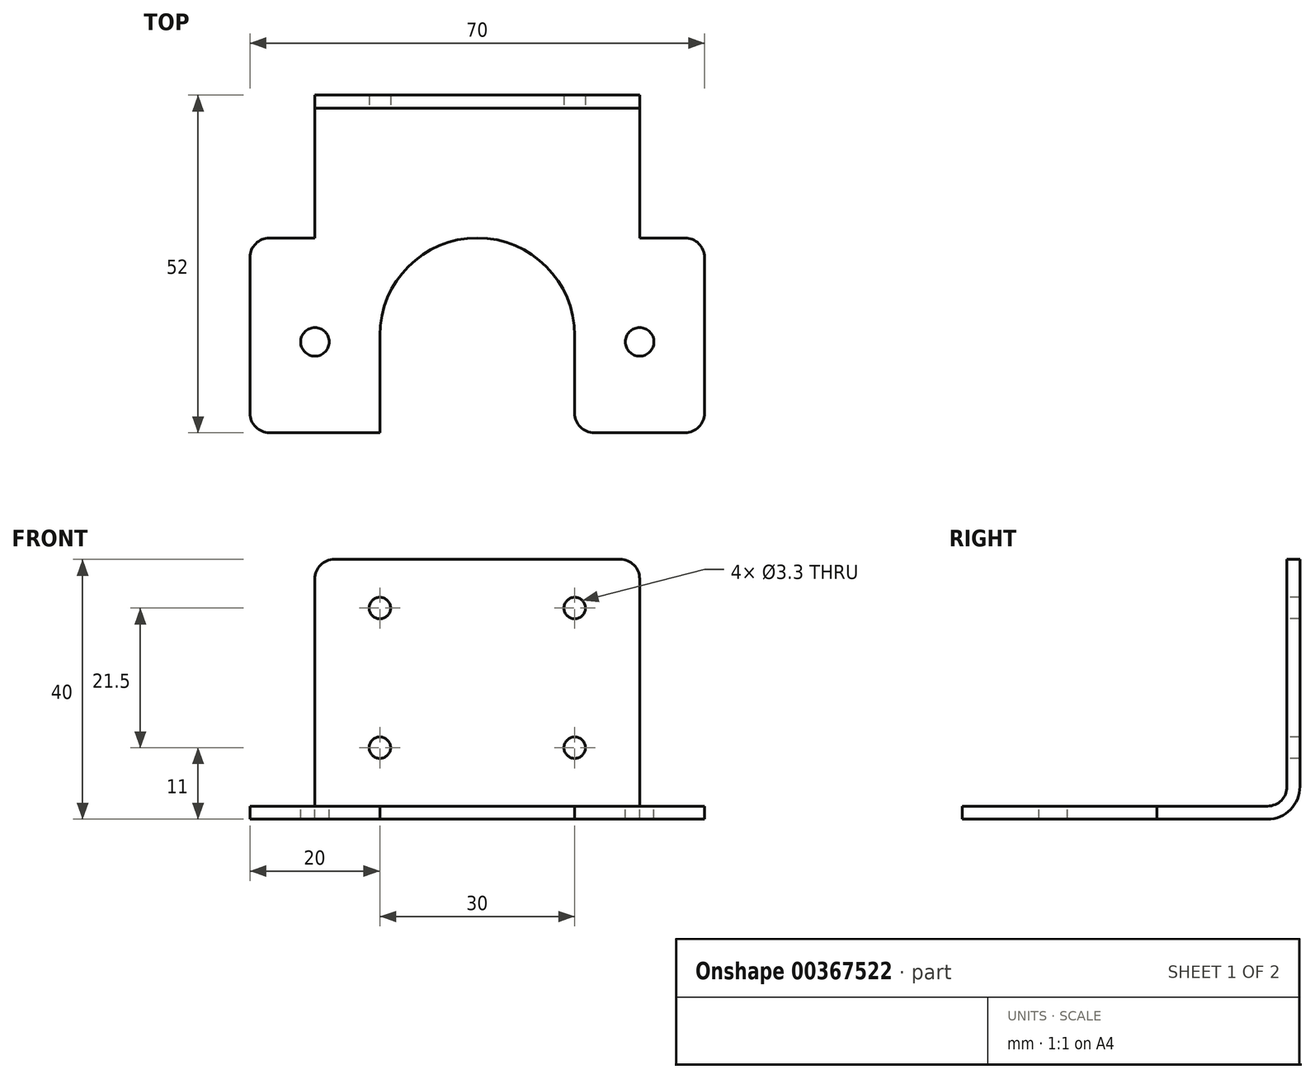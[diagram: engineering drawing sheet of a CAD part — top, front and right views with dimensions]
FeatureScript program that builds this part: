
annotation { "Feature Type Name" : "Feature", "Feature Type Description" : "" }
export const myFeature = defineFeature(function(context is Context, id is Id, definition is map)
    precondition{}
    {
        {
            var Q0;
            Q0=qCreatedBy(makeId("Right.planeOp"),FACE);
            var sketch = newSketch(context, id + "F0", { "sketchPlane" : qUnion([Q0])});
            skLineSegment(sketch, "E0", {"start": v(0, 5) * mm, "end": v(0, 40) * mm});
            skLineSegment(sketch, "E1", {"start": v(-5, 0) * mm, "end": v(-52, 0) * mm});
            skPoint(sketch, "E2.visualSharp", {"position": v(0, 0) * mm});
            skArc(sketch, "E2.filletArc", {"start": v(-5, 0) * mm, "mid": v(-1.46, 1.46) * mm, "end": v(0, 5) * mm});
            skLineSegment(sketch, "E3.0", {"start": v(-2, 5) * mm, "end": v(-2, 40) * mm});
            skArc(sketch, "E3.1", {"start": v(-5, 2) * mm, "mid": v(-2.88, 2.88) * mm, "end": v(-2, 5) * mm});
            skLineSegment(sketch, "E3.2", {"start": v(-5, 2) * mm, "end": v(-52, 2) * mm});
            skLineSegment(sketch, "E4", {"start": v(-52, 2) * mm, "end": v(-52, 0) * mm});
            skLineSegment(sketch, "E5", {"start": v(-2, 40) * mm, "end": v(0, 40) * mm});
            skSolve(sketch);
        }
        {
            var Q0;
            Q0=makeQuery(id+"F0.imprint","IMPRINT",FACE,{"disambiguationData":[TD([[makeQuery(id+"F0.imprint","IMPRINT",EDGE,{"derivedFrom":sQuery(id+"F0.wireOp",EDGE,"E0")}),1.0]])]});
            extrude(context, id + "F1", {"entities" : qUnion([Q0]), "endBound" : BoundingType.SYMMETRIC, "depth" : 50 * mm});
        }
        {
            var Q0;
            Q0=makeQuery(id+"F1.opExtrude","SWEPT_FACE",FACE,{"disambiguationData":[OSD([sQuery(id+"F0.wireOp",EDGE,"E3.0")])]});
            var sketch = newSketch(context, id + "F2", { "sketchPlane" : qUnion([Q0])});
            skLineSegment(sketch, "E6.bottom", {"start": v(15, 32.5) * mm, "end": v(-15, 32.5) * mm});
            skLineSegment(sketch, "E6.top", {"start": v(15, 11) * mm, "end": v(-15, 11) * mm});
            skLineSegment(sketch, "E6.left", {"start": v(15, 32.5) * mm, "end": v(15, 11) * mm});
            skLineSegment(sketch, "E6.right", {"start": v(-15, 32.5) * mm, "end": v(-15, 11) * mm});
            skPoint(sketch, "E6.middle", {"position": v(0, 21.75) * mm});
            skSolve(sketch);
        }
        {
            var Q0;
            Q0=sQuery(id+"F2.wireOp",VERTEX,"E6.right.start");
            var Q1;
            Q1=sQuery(id+"F2.wireOp",VERTEX,"E6.top.end");
            var Q2;
            Q2=sQuery(id+"F2.wireOp",VERTEX,"E6.left.end");
            var Q3;
            Q3=sQuery(id+"F2.wireOp",VERTEX,"E6.left.start");
            var Q4;
            Q4=makeQuery(id+"F1.opExtrude","SWEPT_BODY",BODY,{"disambiguationData":[OSD([sQuery(id+"F0.wireOp",EDGE,"E0"),sQuery(id+"F0.wireOp",EDGE,"E1"),sQuery(id+"F0.wireOp",EDGE,"E2.filletArc"),sQuery(id+"F0.wireOp",EDGE,"E3.0"),sQuery(id+"F0.wireOp",EDGE,"E3.1"),sQuery(id+"F0.wireOp",EDGE,"E3.2"),sQuery(id+"F0.wireOp",EDGE,"E4"),sQuery(id+"F0.wireOp",EDGE,"E5")])]});
            hole(context, id + "F3", {"style" : HoleStyle.SIMPLE, "endStyle" : HoleEndStyle.THROUGH, "standardTappedOrClearance" : lookupTablePath({ "standard" : "ISO", "fit" : "Normal", "size" : "M3", "type" : "Clearance" }), "standardBlindInLast" : lookupTablePath({ "fit" : "Standard", "standard" : "ISO", "size" : "M3", "type" : "Clearance" }), "holeDiameter" : 3.3 * mm, "tappedDepth" : 12 * mm, "tapClearance" : 3, "locations" : qUnion([Q0, Q1, Q2, Q3]), "scope" : qUnion([Q4])});
        }
        {
            var Q0;
            Q0=makeQuery(id+"F1.opExtrude","SWEPT_FACE",FACE,{"disambiguationData":[OSD([sQuery(id+"F0.wireOp",EDGE,"E3.2")])]});
            var sketch = newSketch(context, id + "F4", { "sketchPlane" : qUnion([Q0])});
            skLineSegment(sketch, "E7.bottom", {"start": v(-25, -52) * mm, "end": v(-35, -52) * mm});
            skLineSegment(sketch, "E7.top", {"start": v(-25, -22) * mm, "end": v(-35, -22) * mm});
            skLineSegment(sketch, "E7.left", {"start": v(-25, -52) * mm, "end": v(-25, -22) * mm});
            skLineSegment(sketch, "E7.right", {"start": v(-35, -52) * mm, "end": v(-35, -22) * mm});
            skLineSegment(sketch, "E8", {"start": v(-25, -38) * mm, "end": v(-35, -38) * mm, "construction": true});
            skLineSegment(sketch, "E9.MirrorCS", {"start": v(25, -52) * mm, "end": v(35, -52) * mm});
            skLineSegment(sketch, "E10.MirrorCS", {"start": v(25, -22) * mm, "end": v(35, -22) * mm});
            skLineSegment(sketch, "E11.MirrorCS", {"start": v(25, -52) * mm, "end": v(25, -22) * mm});
            skLineSegment(sketch, "E12.MirrorCS", {"start": v(35, -52) * mm, "end": v(35, -22) * mm});
            skLineSegment(sketch, "E13.MirrorCS", {"start": v(25, -38) * mm, "end": v(35, -38) * mm, "construction": true});
            skCircle(sketch, "E14", {"center": v(0, -37) * mm, "radius": 15 * mm});
            skLineSegment(sketch, "E15", {"start": v(-15, -37) * mm, "end": v(-15, -52) * mm});
            skLineSegment(sketch, "E16", {"start": v(15, -37) * mm, "end": v(15, -52) * mm});
            skSolve(sketch);
        }
        {
            var Q0;
            Q0=makeQuery(id+"F4.imprint","IMPRINT",FACE,{"disambiguationData":[TD([[makeQuery(id+"F4.imprint","IMPRINT",EDGE,{"derivedFrom":sQuery(id+"F4.wireOp",EDGE,"E7.bottom")}),-1.0]])]});
            var Q1;
            Q1=makeQuery(id+"F4.imprint","IMPRINT",FACE,{"disambiguationData":[TD([[makeQuery(id+"F4.imprint","IMPRINT",EDGE,{"derivedFrom":sQuery(id+"F4.wireOp",EDGE,"E9.MirrorCS")}),1.0]])]});
            var Q2;
            Q2=makeQuery(id+"F1.opExtrude","SWEPT_FACE",FACE,{"disambiguationData":[OSD([sQuery(id+"F0.wireOp",EDGE,"E1")])]});
            extrude(context, id + "F5", {"entities" : qUnion([Q0, Q1]), "operationType" : NewBodyOperationType.ADD, "endBound" : BoundingType.UP_TO_SURFACE, "oppositeDirection" : true, "endBoundEntityFace" : qUnion([Q2]), "depth" : 25 * mm});
        }
        {
            var Q0;
            Q0=sQuery(id+"F4.wireOp",VERTEX,"E8.start");
            var Q1;
            Q1=sQuery(id+"F4.wireOp",VERTEX,"E13.MirrorCS.start");
            var Q2;
            Q2=makeQuery(id+"F1.opExtrude","SWEPT_BODY",BODY,{"disambiguationData":[OSD([sQuery(id+"F0.wireOp",EDGE,"E0"),sQuery(id+"F0.wireOp",EDGE,"E1"),sQuery(id+"F0.wireOp",EDGE,"E2.filletArc"),sQuery(id+"F0.wireOp",EDGE,"E3.0"),sQuery(id+"F0.wireOp",EDGE,"E3.1"),sQuery(id+"F0.wireOp",EDGE,"E3.2"),sQuery(id+"F0.wireOp",EDGE,"E4"),sQuery(id+"F0.wireOp",EDGE,"E5")])]});
            hole(context, id + "F6", {"style" : HoleStyle.SIMPLE, "endStyle" : HoleEndStyle.THROUGH, "standardTappedOrClearance" : lookupTablePath({ "standard" : "ISO", "fit" : "Normal", "size" : "M4", "type" : "Clearance" }), "standardBlindInLast" : lookupTablePath({ "fit" : "Standard", "standard" : "ISO", "size" : "M4", "type" : "Clearance" }), "holeDiameter" : 4.4 * mm, "tappedDepth" : 12 * mm, "tapClearance" : 3, "locations" : qUnion([Q0, Q1]), "scope" : qUnion([Q2])});
        }
        {
            var Q0;
            {var subQ0=sQuery(id+"F4.wireOp",EDGE,"E14");var subQ1=makeQuery(id+"F4.imprint","INTERSECT",VERTEX,{"derivedFrom":[subQ0,sQuery(id+"F4.wireOp",EDGE,"E15")]});Q0=makeQuery(id+"F4.imprint","IMPRINT",FACE,{"disambiguationData":[TD([[makeQuery(id+"F4.imprint","IMPRINT",EDGE,{"disambiguationData":[TD([[subQ1,1.0]])],"derivedFrom":subQ0}),1.0]])]});}
            var Q1;
            {var subQ0=sQuery(id+"F4.wireOp",EDGE,"E15");Q1=makeQuery(id+"F4.imprint","IMPRINT",FACE,{"disambiguationData":[TD([[makeQuery(id+"F4.imprint","IMPRINT",EDGE,{"derivedFrom":subQ0}),1.0]])]});}
            var Q2;
            {var subQ0=sQuery(id+"F4.wireOp",EDGE,"E16");Q2=makeQuery(id+"F4.imprint","IMPRINT",FACE,{"disambiguationData":[TD([[makeQuery(id+"F4.imprint","IMPRINT",EDGE,{"derivedFrom":subQ0}),-1.0]])]});}
            extrude(context, id + "F7", {"entities" : qUnion([Q0, Q1, Q2]), "operationType" : NewBodyOperationType.REMOVE, "endBound" : BoundingType.UP_TO_NEXT, "oppositeDirection" : true, "depth" : 25 * mm});
        }
        {
            var Q0;
            Q0=makeQuery(id+"F7.boolean.opBoolean","COPY",EDGE,{"derivedFrom":makeQuery(id+"F7.opExtrude","SWEPT_EDGE",EDGE,{"disambiguationData":[OSD([sQuery(id+"F0.wireOp",EDGE,"E3.2"),sQuery(id+"F0.wireOp",EDGE,"E4"),sQuery(id+"F4.wireOp",EDGE,"E15")])]})});
            var Q1;
            Q1=makeQuery(id+"F5.opExtrude","SWEPT_EDGE",EDGE,{"disambiguationData":[OSD([sQuery(id+"F4.wireOp",EDGE,"E7.bottom"),sQuery(id+"F4.wireOp",EDGE,"E7.right")])]});
            var Q2;
            Q2=makeQuery(id+"F5.opExtrude","SWEPT_EDGE",EDGE,{"disambiguationData":[OSD([sQuery(id+"F4.wireOp",EDGE,"E7.top"),sQuery(id+"F4.wireOp",EDGE,"E7.right")])]});
            var Q3;
            Q3=makeQuery(id+"F5.opExtrude","SWEPT_EDGE",EDGE,{"disambiguationData":[OSD([sQuery(id+"F0.wireOp",EDGE,"E3.2"),sQuery(id+"F4.wireOp",EDGE,"E7.top"),sQuery(id+"F4.wireOp",EDGE,"E7.left")])]});
            var Q4;
            Q4=makeQuery(id+"F1.opExtrude","CAP_EDGE",EDGE,{"disambiguationData":[OSD([sQuery(id+"F0.wireOp",EDGE,"E5")])],"isStart":true});
            var Q5;
            Q5=makeQuery(id+"F7.boolean.opBoolean","COPY",EDGE,{"derivedFrom":makeQuery(id+"F7.opExtrude","SWEPT_EDGE",EDGE,{"disambiguationData":[OSD([sQuery(id+"F0.wireOp",EDGE,"E3.2"),sQuery(id+"F0.wireOp",EDGE,"E4"),sQuery(id+"F4.wireOp",EDGE,"E16")])]})});
            var Q6;
            Q6=makeQuery(id+"F5.opExtrude","SWEPT_EDGE",EDGE,{"disambiguationData":[OSD([sQuery(id+"F4.wireOp",EDGE,"E9.MirrorCS"),sQuery(id+"F4.wireOp",EDGE,"E12.MirrorCS")])]});
            var Q7;
            Q7=makeQuery(id+"F5.opExtrude","SWEPT_EDGE",EDGE,{"disambiguationData":[OSD([sQuery(id+"F4.wireOp",EDGE,"E10.MirrorCS"),sQuery(id+"F4.wireOp",EDGE,"E12.MirrorCS")])]});
            var Q8;
            Q8=makeQuery(id+"F5.opExtrude","SWEPT_EDGE",EDGE,{"disambiguationData":[OSD([sQuery(id+"F0.wireOp",EDGE,"E3.2"),sQuery(id+"F4.wireOp",EDGE,"E10.MirrorCS"),sQuery(id+"F4.wireOp",EDGE,"E11.MirrorCS")])]});
            var Q9;
            Q9=makeQuery(id+"F1.opExtrude","CAP_EDGE",EDGE,{"disambiguationData":[OSD([sQuery(id+"F0.wireOp",EDGE,"E5")])],"isStart":false});
            fillet(context, id + "F8", {"entities" : qUnion([Q0, Q1, Q2, Q3, Q4, Q5, Q6, Q7, Q8, Q9]), "radius" : 3 * mm, "tangentPropagation" : true, "allowEdgeOverflow" : false});
        }
    });
